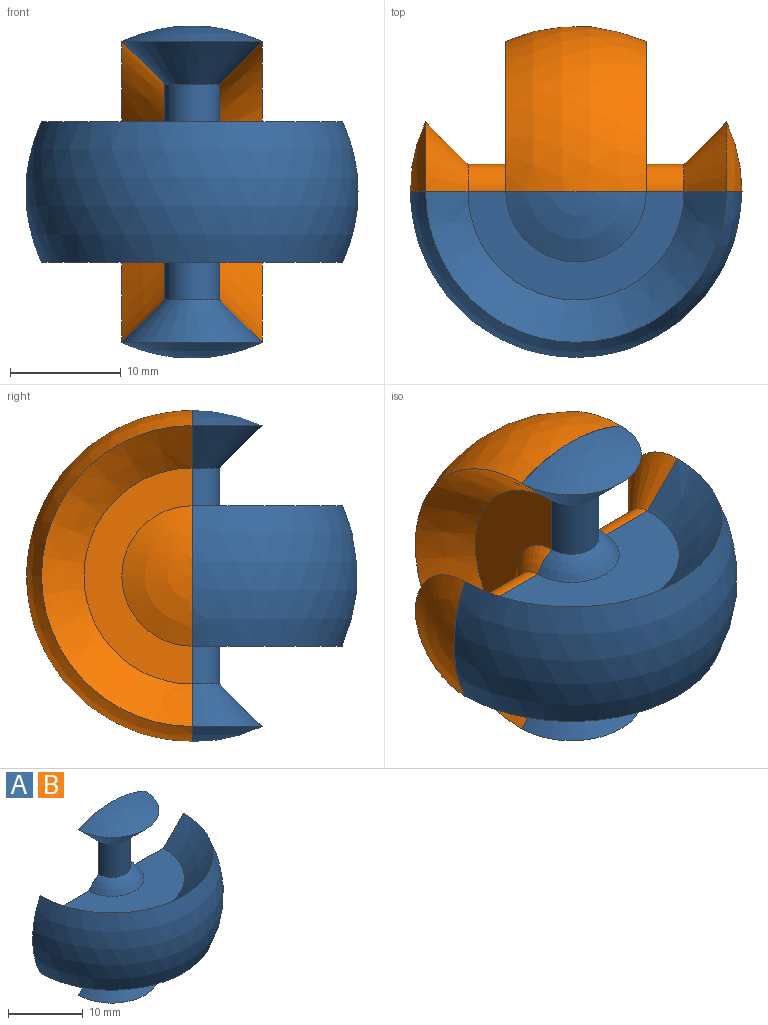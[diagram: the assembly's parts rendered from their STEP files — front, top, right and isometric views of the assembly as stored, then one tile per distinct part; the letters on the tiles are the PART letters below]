
ASSEMBLY  parts=2 mates=1
PART A: 22 faces, bbox 30x15x30 mm
  f0: sphere r=15mm, area 66.2mm2, adj f1,f13
  f1: cone r=2.5mm half-angle=45deg, axis (0,0,-1), area 75.3mm2, adj f0,f2,f13
  f2: cylinder r=2.5mm len=5.43mm, axis (0,0,1), area 42.6mm2, adj f1,f3,f13
  f3: sphere r=5mm, area 28.7mm2, adj f2,f4,f13
  f4: plane 19.52x9.76mm, normal (0,0,-1), area 120.1mm2, adj f3,f5,f13
  f5: cone r=9.76mm half-angle=45deg, axis (0,0,-1), area 199.1mm2, adj f4,f6,f13
  f6: sphere r=15mm, area 597.3mm2, adj f5,f7,f13
  f7: cone r=9.76mm half-angle=45deg, axis (0,0,1), area 199.1mm2, adj f6,f8,f13
  f8: plane 19.52x9.76mm, normal (0,0,1), area 120.1mm2, adj f7,f9,f13
  f9: sphere r=5mm, area 28.7mm2, adj f8,f10,f13
  f10: cylinder r=2.5mm len=5.43mm, axis (0,0,1), area 42.6mm2, adj f9,f11,f13
  f11: cone r=2.5mm half-angle=45deg, axis (0,0,1), area 75.3mm2, adj f10,f12,f13
  f12: sphere r=15mm, area 66.2mm2, adj f11,f13
  f13: plane 30x30mm, normal (0,1,0), area 333.4mm2, adj f0,f1,f2,f3,f4,f5,f6,f7
  f14: cylinder r=1.5mm len=3mm, axis (0,1,0), area 28.3mm2, adj f13,f15
  f15: plane 3x3mm, normal (0,1,0), area 7.1mm2, adj f14
  f16: cylinder r=1.5mm len=3mm, axis (0,1,0), area 28.3mm2, adj f13,f17
  f17: plane 3x3mm, normal (0,1,0), area 7.1mm2, adj f16
  f18: cylinder r=1.5mm len=3mm, axis (0,1,0), area 28.3mm2, adj f13,f19
  f19: plane 3x3mm, normal (0,1,0), area 7.1mm2, adj f18
  f20: cylinder r=1.5mm len=3mm, axis (0,1,0), area 28.3mm2, adj f13,f21
  f21: plane 3x3mm, normal (0,1,0), area 7.1mm2, adj f20
PART B: same geometry as A
PLACE A t=(-12.6,-2.47,-4.04)mm
PLACE B rot(axis=(-0.71,0,0.71),180deg) t=(-12.6,-2.47,-4.04)mm
MATE fastened B.f13 <-> A.f13  axis (0,-1,0) through (-12.6,-2.47,-4.04)mm
